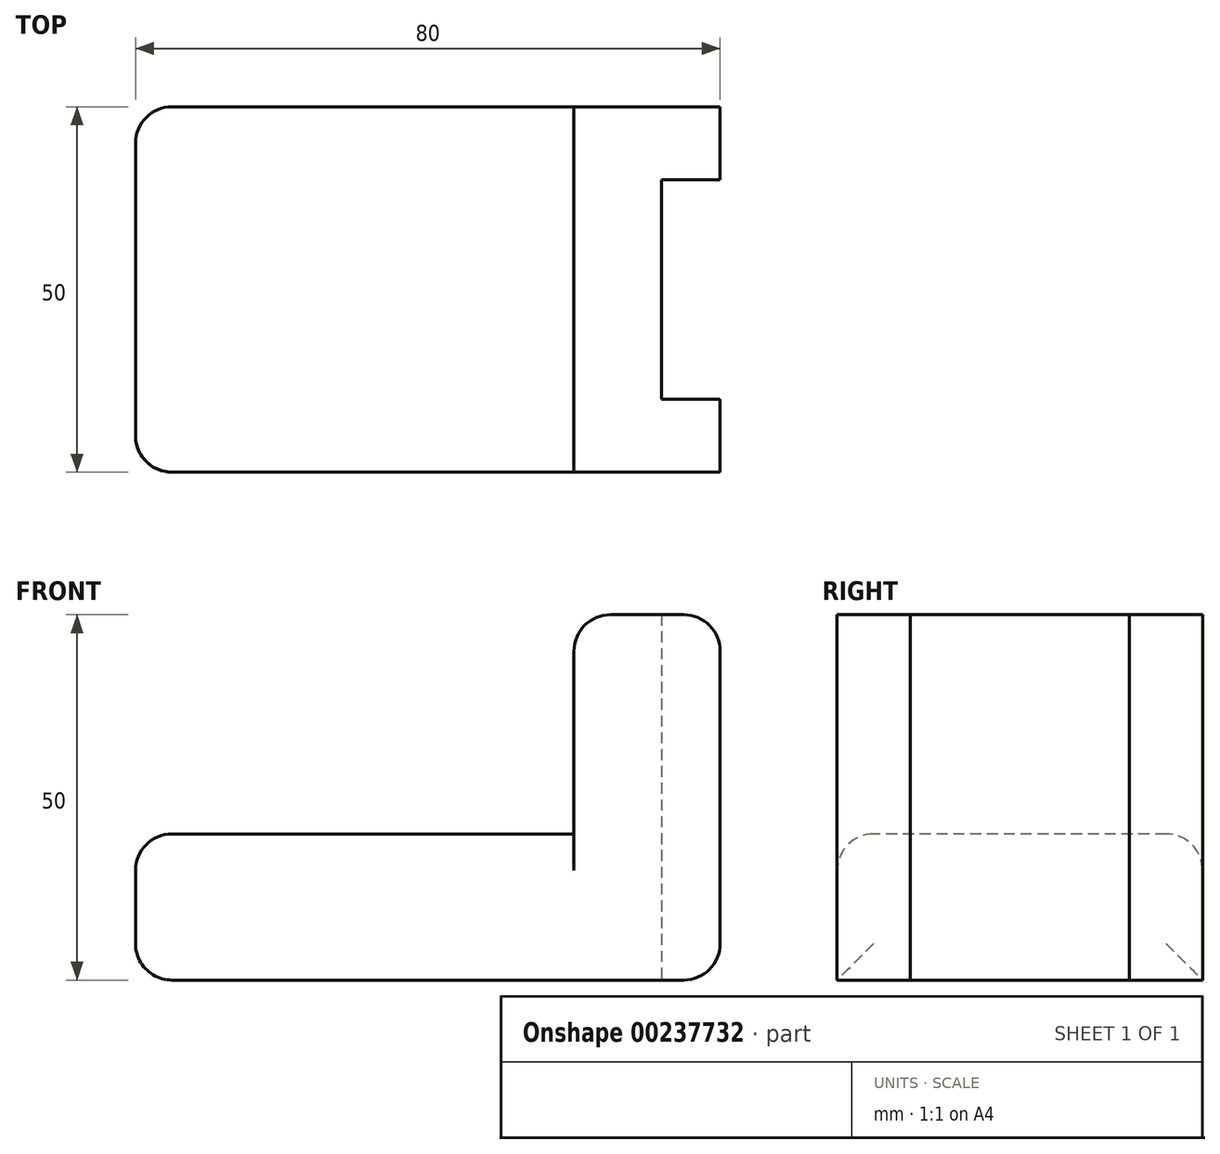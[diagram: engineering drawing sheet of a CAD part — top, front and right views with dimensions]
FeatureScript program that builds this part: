
annotation { "Feature Type Name" : "Feature", "Feature Type Description" : "" }
export const myFeature = defineFeature(function(context is Context, id is Id, definition is map)
    precondition{}
    {
        {
            var Q0;
            Q0=qCreatedBy(makeId("Top.planeOp"),FACE);
            var sketch = newSketch(context, id + "F0", { "sketchPlane" : qUnion([Q0])});
            skLineSegment(sketch, "E0.bottom", {"start": v(-72, 69.3) * mm, "end": v(-12, 69.3) * mm});
            skLineSegment(sketch, "E0.top", {"start": v(-72, 19.3) * mm, "end": v(-12, 19.3) * mm});
            skLineSegment(sketch, "E0.left", {"start": v(-72, 69.3) * mm, "end": v(-72, 19.3) * mm});
            skLineSegment(sketch, "E0.right", {"start": v(-12, 69.3) * mm, "end": v(-12, 19.3) * mm});
            skLineSegment(sketch, "E1.bottom", {"start": v(-12, 69.3) * mm, "end": v(8, 69.3) * mm});
            skLineSegment(sketch, "E1.top", {"start": v(-12, 19.3) * mm, "end": v(8, 19.3) * mm});
            skLineSegment(sketch, "E1.right", {"start": v(8, 69.3) * mm, "end": v(8, 19.3) * mm});
            skLineSegment(sketch, "E2.bottom", {"start": v(0, 59.3) * mm, "end": v(8, 59.3) * mm});
            skLineSegment(sketch, "E2.top", {"start": v(0, 29.3) * mm, "end": v(8, 29.3) * mm});
            skLineSegment(sketch, "E2.left", {"start": v(0, 59.3) * mm, "end": v(0, 29.3) * mm});
            skLineSegment(sketch, "E2.right", {"start": v(8, 59.3) * mm, "end": v(8, 29.3) * mm});
            skSolve(sketch);
        }
        {
            var Q0;
            Q0=makeQuery(id+"F0.imprint","IMPRINT",FACE,{"disambiguationData":[TD([[makeQuery(id+"F0.imprint","IMPRINT",EDGE,{"derivedFrom":sQuery(id+"F0.wireOp",EDGE,"E0.bottom")}),-1.0]])]});
            extrude(context, id + "F1", {"entities" : qUnion([Q0]), "depth" : 20 * mm});
        }
        {
            var Q0;
            {var subQ2=sQuery(id+"F0.wireOp",EDGE,"E1.bottom");Q0=makeQuery(id+"F0.imprint","IMPRINT",FACE,{"disambiguationData":[TD([[makeQuery(id+"F0.imprint","IMPRINT",EDGE,{"derivedFrom":subQ2}),-1.0]])]});}
            extrude(context, id + "F2", {"entities" : qUnion([Q0]), "operationType" : NewBodyOperationType.ADD, "depth" : 50 * mm});
        }
        {
            var Q0;
            Q0=makeQuery(id+"F1.opExtrude","CAP_EDGE",EDGE,{"disambiguationData":[OSD([sQuery(id+"F0.wireOp",EDGE,"E0.left")])],"isStart":false});
            fillet(context, id + "F3", {"entities" : qUnion([Q0]), "radius" : 5 * mm, "tangentPropagation" : true, "allowEdgeOverflow" : false});
        }
        {
            var Q0;
            Q0=makeQuery(id+"F2.opExtrude","CAP_EDGE",EDGE,{"disambiguationData":[OSD([sQuery(id+"F0.wireOp",EDGE,"E0.right")])],"isStart":false});
            fillet(context, id + "F4", {"entities" : qUnion([Q0]), "radius" : 5 * mm, "tangentPropagation" : true, "allowEdgeOverflow" : false});
        }
        {
            var Q0;
            Q0=makeQuery(id+"F1.opExtrude","SWEPT_FACE",FACE,{"disambiguationData":[OSD([sQuery(id+"F0.wireOp",EDGE,"E0.left")])]});
            var Q1;
            {var subQ0=sQuery(id+"F0.wireOp",EDGE,"E0.left");Q1=makeQuery(id+"F3.opFillet","BLEND_EDGE",EDGE,{"blendedFrom":[makeQuery(id+"F1.opExtrude","CAP_EDGE",EDGE,{"disambiguationData":[OSD([subQ0])],"isStart":false}),makeQuery(id+"F1.opExtrude","SWEPT_FACE",FACE,{"disambiguationData":[OSD([subQ0])]})],"blendedInto":[makeQuery(id+"F1.opExtrude","SWEPT_FACE",FACE,{"disambiguationData":[OSD([subQ0])]})]});}
            fillet(context, id + "F5", {"entities" : qUnion([Q0, Q1]), "radius" : 5 * mm, "tangentPropagation" : true, "allowEdgeOverflow" : false});
        }
        {
            var Q0;
            {var subQ0=sQuery(id+"F0.wireOp",EDGE,"E1.right");Q0=makeQuery(id+"F2.opExtrude","CAP_EDGE",EDGE,{"disambiguationData":[OSD([subQ0]),TDD([makeQuery(id+"F0.imprint","IMPRINT",EDGE,{"disambiguationData":[TD([[makeQuery(id+"F0.imprint","INTERSECT",VERTEX,{"derivedFrom":[sQuery(id+"F0.wireOp",EDGE,"E1.top"),subQ0]}),1.0]])],"derivedFrom":subQ0})])],"isStart":false});}
            var Q1;
            {var subQ0=sQuery(id+"F0.wireOp",EDGE,"E1.right");Q1=makeQuery(id+"F2.opExtrude","CAP_EDGE",EDGE,{"disambiguationData":[OSD([subQ0]),TDD([makeQuery(id+"F0.imprint","IMPRINT",EDGE,{"disambiguationData":[TD([[makeQuery(id+"F0.imprint","INTERSECT",VERTEX,{"derivedFrom":[sQuery(id+"F0.wireOp",EDGE,"E1.bottom"),subQ0]}),-1.0]])],"derivedFrom":subQ0})])],"isStart":false});}
            fillet(context, id + "F6", {"entities" : qUnion([Q0, Q1]), "radius" : 5 * mm, "tangentPropagation" : true, "allowEdgeOverflow" : false});
        }
        {
            var Q0;
            {var subQ0=sQuery(id+"F0.wireOp",EDGE,"E1.right");Q0=makeQuery(id+"F2.opExtrude","CAP_EDGE",EDGE,{"disambiguationData":[OSD([subQ0]),TDD([makeQuery(id+"F0.imprint","IMPRINT",EDGE,{"disambiguationData":[TD([[makeQuery(id+"F0.imprint","INTERSECT",VERTEX,{"derivedFrom":[sQuery(id+"F0.wireOp",EDGE,"E1.top"),subQ0]}),1.0]])],"derivedFrom":subQ0})])],"isStart":true});}
            var Q1;
            {var subQ0=sQuery(id+"F0.wireOp",EDGE,"E1.right");Q1=makeQuery(id+"F2.opExtrude","CAP_EDGE",EDGE,{"disambiguationData":[OSD([subQ0]),TDD([makeQuery(id+"F0.imprint","IMPRINT",EDGE,{"disambiguationData":[TD([[makeQuery(id+"F0.imprint","INTERSECT",VERTEX,{"derivedFrom":[sQuery(id+"F0.wireOp",EDGE,"E1.bottom"),subQ0]}),-1.0]])],"derivedFrom":subQ0})])],"isStart":true});}
            fillet(context, id + "F7", {"entities" : qUnion([Q0, Q1]), "radius" : 5 * mm, "tangentPropagation" : true, "allowEdgeOverflow" : false});
        }
    });
